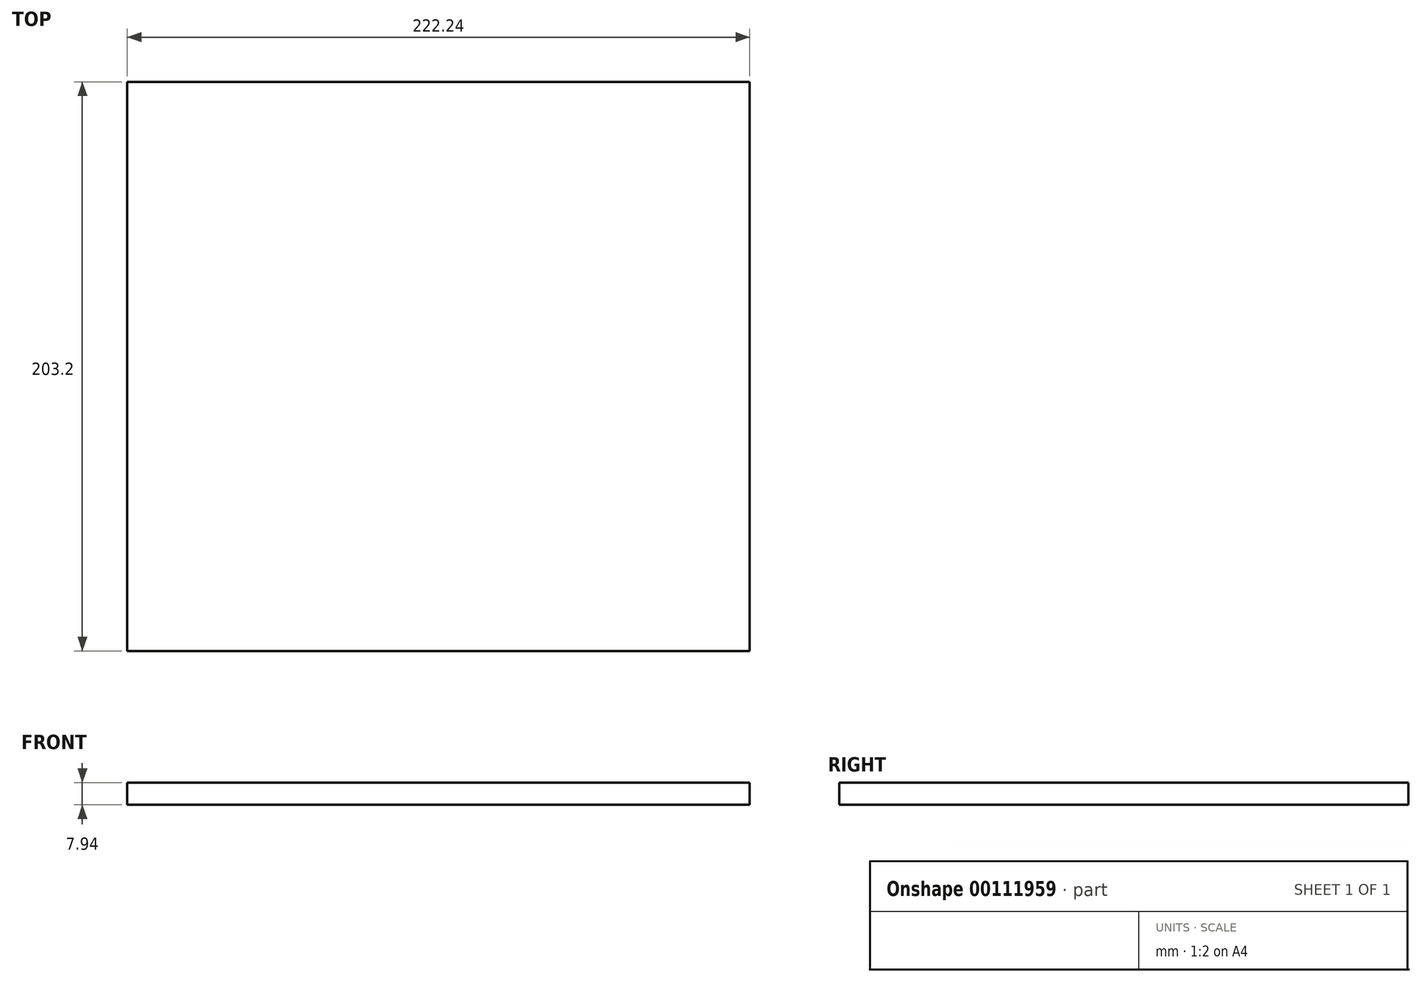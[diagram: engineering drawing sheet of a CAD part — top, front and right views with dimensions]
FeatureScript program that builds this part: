
annotation { "Feature Type Name" : "Feature", "Feature Type Description" : "" }
export const myFeature = defineFeature(function(context is Context, id is Id, definition is map)
    precondition{}
    {
        {
            var Q0;
            Q0=qCreatedBy(makeId("Top.planeOp"),FACE);
            var sketch = newSketch(context, id + "F0", { "sketchPlane" : qUnion([Q0])});
            skLineSegment(sketch, "E0.bottom", {"start": v(-111.13, 101.6) * mm, "end": v(111.13, 101.6) * mm});
            skLineSegment(sketch, "E0.top", {"start": v(-111.13, -101.6) * mm, "end": v(111.13, -101.6) * mm});
            skLineSegment(sketch, "E0.left", {"start": v(-111.13, 101.6) * mm, "end": v(-111.13, -101.6) * mm});
            skLineSegment(sketch, "E0.right", {"start": v(111.13, 101.6) * mm, "end": v(111.13, -101.6) * mm});
            skPoint(sketch, "E0.middle", {"position": v(0, 0) * mm});
            skSolve(sketch);
        }
        {
            var Q0;
            Q0=makeQuery(id+"F0.imprint","IMPRINT",FACE,{"disambiguationData":[TD([[makeQuery(id+"F0.imprint","IMPRINT",EDGE,{"derivedFrom":sQuery(id+"F0.wireOp",EDGE,"E0.bottom")}),-1.0]])]});
            extrude(context, id + "F1", {"entities" : qUnion([Q0]), "depth" : 7.94 * mm});
        }
    });
